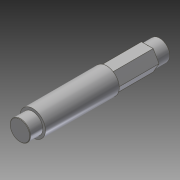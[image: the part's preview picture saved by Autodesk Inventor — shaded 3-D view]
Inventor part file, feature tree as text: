
AUTODESK INVENTOR PART (.ipt)
format: ipt  version: 2014 SP1 (Build 180222100, 222)  size: 101,376 bytes
history: native  units: in
note: dims shown in document units (in); Inventor stores cm internally (conversion verified against a paired STEP export)
features: chamfer x1, other x1, imported_body x1
ambient origin geometry x8: Origin, YZ Plane, XZ Plane, XY Plane, X Axis, Y Axis, Z Axis, Center Point
bodies: Body1 (feature_tree)
feature tree (3):
  chamfer  "Chamfer1"  [1 undecoded]
  other  "217-3433-003 Rev1.ipt1"
  imported_body  "Base1"
note: 1 required parameter value undecoded (feature->parameter linkage not recoverable at this tier; creation-order binding heuristic only, values carry confidence <= 0.55)
